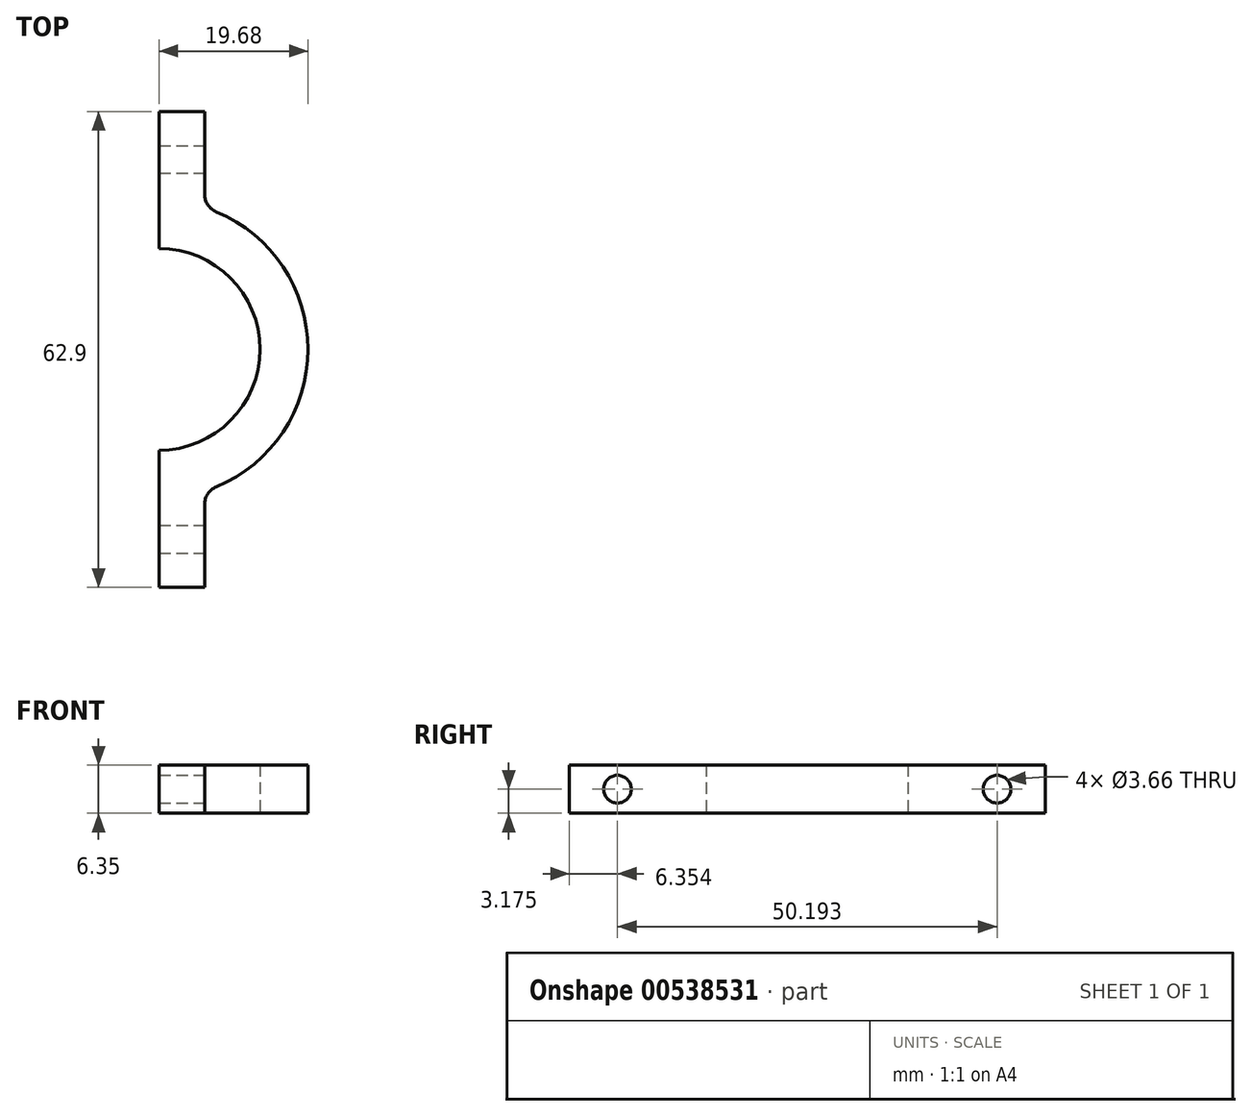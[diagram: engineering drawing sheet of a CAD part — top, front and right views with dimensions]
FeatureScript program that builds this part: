
annotation { "Feature Type Name" : "Feature", "Feature Type Description" : "" }
export const myFeature = defineFeature(function(context is Context, id is Id, definition is map)
    precondition{}
    {
        {
            var Q0;
            Q0=qCreatedBy(makeId("Top.planeOp"),FACE);
            var sketch = newSketch(context, id + "F0", { "sketchPlane" : qUnion([Q0])});
            skArc(sketch, "E0", {"start": v(0, -13.34) * mm, "mid": v(13.34, 0) * mm, "end": v(0, 13.34) * mm});
            skArc(sketch, "E1", {"start": v(6, -18.75) * mm, "mid": v(19.69, 0) * mm, "end": v(6, 18.75) * mm});
            skLineSegment(sketch, "E2.bottom", {"start": v(6, -31.45) * mm, "end": v(0, -31.45) * mm});
            skLineSegment(sketch, "E2.top", {"start": v(6, 31.45) * mm, "end": v(0, 31.45) * mm});
            skLineSegment(sketch, "E2.left", {"start": v(6, -31.45) * mm, "end": v(6, -18.75) * mm});
            skLineSegment(sketch, "E3", {"start": v(0, 31.45) * mm, "end": v(0, 13.34) * mm});
            skLineSegment(sketch, "E4.trimOffspring", {"start": v(6, 18.75) * mm, "end": v(6, 31.45) * mm});
            skPoint(sketch, "E5.orphan", {"position": v(-6, -31.45) * mm});
            skPoint(sketch, "E6.orphan", {"position": v(-6, 31.45) * mm});
            skLineSegment(sketch, "E7.trimOffspring", {"start": v(0, -13.34) * mm, "end": v(0, -31.45) * mm});
            skSolve(sketch);
        }
        {
            var Q0;
            Q0=makeQuery(id+"F0.imprint","IMPRINT",FACE,{"disambiguationData":[TD([[makeQuery(id+"F0.imprint","IMPRINT",EDGE,{"derivedFrom":sQuery(id+"F0.wireOp",EDGE,"E0")}),-1.0]])]});
            extrude(context, id + "F1", {"entities" : qUnion([Q0]), "depth" : 6.35 * mm, "offsetDistance" : 25.4 * mm});
        }
        {
            var Q0;
            Q0=makeQuery(id+"F1.opExtrude","SWEPT_FACE",FACE,{"disambiguationData":[OSD([sQuery(id+"F0.wireOp",EDGE,"E2.left")])]});
            var sketch = newSketch(context, id + "F2", { "sketchPlane" : qUnion([Q0])});
            skLineSegment(sketch, "E8", {"start": v(-25.1, 0) * mm, "end": v(-25.1, 6.35) * mm, "construction": true});
            skLineSegment(sketch, "E9", {"start": v(-31.45, 3.18) * mm, "end": v(-18.75, 3.18) * mm, "construction": true});
            skCircle(sketch, "E10", {"center": v(-25.1, 3.18) * mm, "radius": 1.83 * mm});
            skSolve(sketch);
        }
        {
            var Q0;
            Q0=makeQuery(id+"F1.opExtrude","SWEPT_FACE",FACE,{"disambiguationData":[OSD([sQuery(id+"F0.wireOp",EDGE,"E4.trimOffspring")])]});
            var sketch = newSketch(context, id + "F3", { "sketchPlane" : qUnion([Q0])});
            skLineSegment(sketch, "E11", {"start": v(25.1, 6.35) * mm, "end": v(25.1, 0) * mm, "construction": true});
            skLineSegment(sketch, "E12", {"start": v(18.75, 3.18) * mm, "end": v(31.45, 3.18) * mm, "construction": true});
            skCircle(sketch, "E13", {"center": v(25.1, 3.18) * mm, "radius": 1.83 * mm});
            skSolve(sketch);
        }
        {
            var Q0;
            Q0=makeQuery(id+"F2.imprint","IMPRINT",FACE,{"disambiguationData":[TD([[makeQuery(id+"F2.imprint","IMPRINT",EDGE,{"derivedFrom":sQuery(id+"F2.wireOp",EDGE,"E10")}),1.0]])]});
            var Q1;
            Q1=makeQuery(id+"F3.imprint","IMPRINT",FACE,{"disambiguationData":[TD([[makeQuery(id+"F3.imprint","IMPRINT",EDGE,{"derivedFrom":sQuery(id+"F3.wireOp",EDGE,"E13")}),1.0]])]});
            var Q2;
            Q2=makeQuery(id+"F1.opExtrude","SWEPT_FACE",FACE,{"disambiguationData":[OSD([sQuery(id+"F0.wireOp",EDGE,"E3")])]});
            extrude(context, id + "F4", {"entities" : qUnion([Q0, Q1]), "operationType" : NewBodyOperationType.REMOVE, "endBound" : BoundingType.UP_TO_SURFACE, "oppositeDirection" : true, "depth" : 25.4 * mm, "endBoundEntityFace" : qUnion([Q2]), "offsetDistance" : 25.4 * mm});
        }
        {
            var Q0;
            Q0=makeQuery(id+"F1.opExtrude","SWEPT_EDGE",EDGE,{"disambiguationData":[OSD([sQuery(id+"F0.wireOp",EDGE,"E1"),sQuery(id+"F0.wireOp",EDGE,"E2.left")])]});
            var Q1;
            Q1=makeQuery(id+"F1.opExtrude","SWEPT_EDGE",EDGE,{"disambiguationData":[OSD([sQuery(id+"F0.wireOp",EDGE,"E1"),sQuery(id+"F0.wireOp",EDGE,"E4.trimOffspring")])]});
            fillet(context, id + "F5", {"entities" : qUnion([Q0, Q1]), "radius" : 2.54 * mm, "tangentPropagation" : true, "allowEdgeOverflow" : false});
        }
    });
